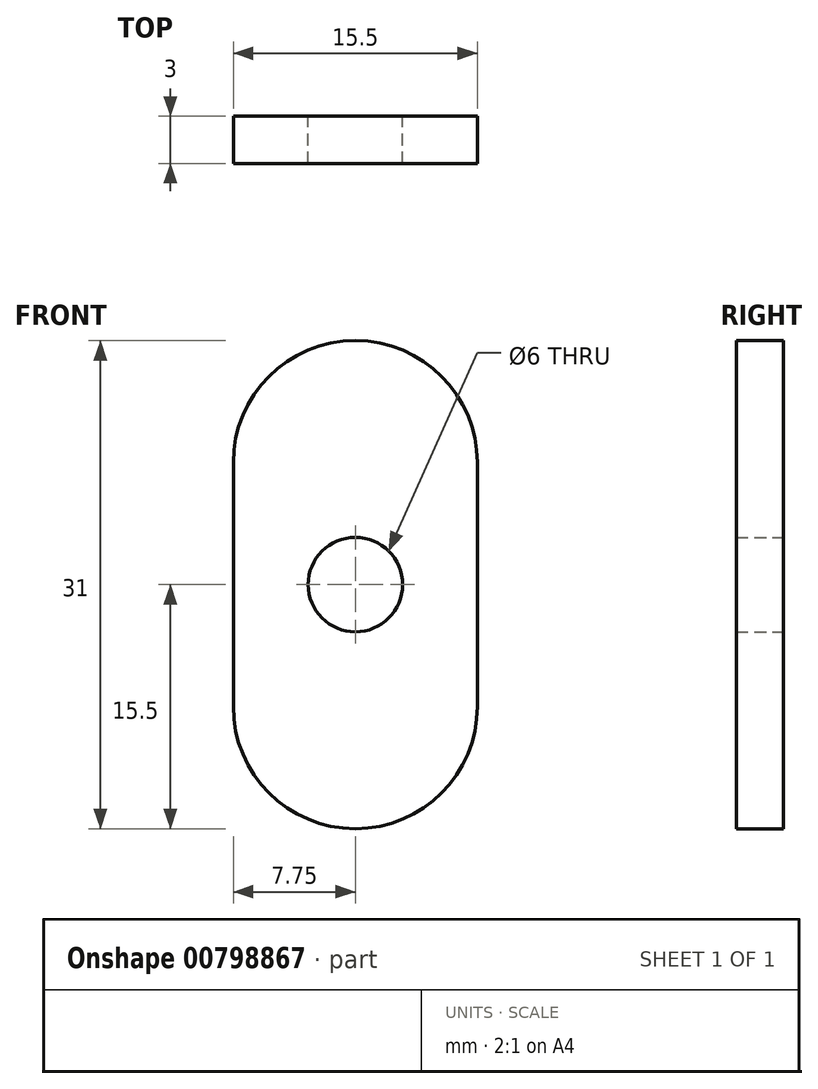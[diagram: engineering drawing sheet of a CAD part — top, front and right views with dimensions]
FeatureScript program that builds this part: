
annotation { "Feature Type Name" : "Feature", "Feature Type Description" : "" }
export const myFeature = defineFeature(function(context is Context, id is Id, definition is map)
    precondition{}
    {
        {
            var Q0;
            Q0=qCreatedBy(makeId("Front.planeOp"),FACE);
            var sketch = newSketch(context, id + "F0", { "sketchPlane" : qUnion([Q0])});
            skLineSegment(sketch, "E0.bottom", {"start": v(-7.75, 7.75) * mm, "end": v(7.75, 7.75) * mm});
            skLineSegment(sketch, "E0.top", {"start": v(-7.75, -7.75) * mm, "end": v(7.75, -7.75) * mm});
            skLineSegment(sketch, "E0.left", {"start": v(-7.75, 7.75) * mm, "end": v(-7.75, -7.75) * mm});
            skLineSegment(sketch, "E0.right", {"start": v(7.75, 7.75) * mm, "end": v(7.75, -7.75) * mm});
            skPoint(sketch, "E0.middle", {"position": v(0, 0) * mm});
            skArc(sketch, "E1", {"start": v(-7.75, 7.75) * mm, "mid": v(0, 15.5) * mm, "end": v(7.75, 7.75) * mm});
            skArc(sketch, "E2", {"start": v(-7.75, -7.75) * mm, "mid": v(0, -15.5) * mm, "end": v(7.75, -7.75) * mm});
            skCircle(sketch, "E3", {"center": v(0, 0) * mm, "radius": 3 * mm});
            skSolve(sketch);
        }
        {
            var Q0;
            Q0 = qSketchRegion(id + "F0", true);
            extrude(context, id + "F1", {"entities" : qUnion([Q0]), "depth" : 3 * mm, "offsetDistance" : 25 * mm});
        }
    });
